# Revit family: Hager-FW-Surface_mounted-IP30-With_Cover-With_DIN-Hosted-AT-de
name_source: partatom
category: Electrical Equipment
units: mm (PartAtom-declared; Revit-internal decimal feet)

## family parameters
Cut with Voids When Loaded = No
Host = Face
Maintain Annotation Orientation = Yes
Panel Configuration = Two Columns, Circuits Across
Part Type = Panelboard
Room Calculation Point = No
Round Connector Dimension = Use Diameter
Shared = No

## types (12) — shared parameters
BC_MODEL_ID = 1554217
BC_OBJECT_ID = 513830
BC_OBJECT_VERSION = #3
Code hager = ADD-EC000214_EU
EF000003 - Montageart = Aufputz
EF000007 - Farbe = weiß
EF000024 - UV-beständig = No
EF000049 - Tiefe = 150 mm
EF000116 - RAL-Nummer = 9010
EF000118 - Mit Montageplatte = No
EF001062 - EMV-Ausführung = No
EF001088 - Anbaumöglichkeit = Yes
EF001134 - DIN-Schiene = Yes
EF004462 - Art der Schließung = sonstige
EF005474 - Schutzart (IP) = IP30
EF006244 - Transparenter Deckel/Tür = No
EF006306 - Mit Schloss = No
EF009212 - Ausführung Deckel = geschlossen
EF015776 - Erdungsklemmenblock = No
EF015777 - Neutralleiterklemmenblock = No
EF015941 - Signaldurchlassende Tür = No
ETIM class code = EC000214
ETIM class name = Small distribution board
HG000001-Anzahl der Spalten = 1
HG000002-Mit tür = Yes
HG000003-Bereich = FW
HG000005-Dicke = 2 mm  [stored 0.00656168 ft]
HG000006-Unterputz = No
HG000009-Doppelflügeligen Tür = No
HG000010-Asymmetrische Türen = No
HG000011-Leere Reihen von unten = No
HG000012-Türschwenkwinkel = 90.00°
HG000013-Tür links = No
HG000014-Tür rechts = Yes
HG000015-Sichtbarkeit der Türöffnung = Yes
HG000016-3D-Türsichtbarkeit = Yes
HG000017-Distanz zwischen den Polen = 18 mm  [stored 0.0590551 ft]
HG000060-RAL-number = 9010
HG000099-Onfly Template ID-de-AT = 507532
Manufacturer = Hager
Name = FW-Surface_mounted-IP30-With_Cover-With_DIN-AT
Name BIM&CO = Electricity
Name hager = ADD_Enclosures_EC000214
Uniformat = Low Tension Service & Dist.
Uniformat code = D501001
zero-valued in all types: Default Elevation, EF000218 - Einbautiefe, EF000332 - Einbauhöhe, EF000846 - Einbaubreite, EF001131 - Innentiefe, HG000007-Anzahl der leeren Spalten, HG000008-Anzahl der leeren Reihen

## per-type parameters (varying)
| type | BC_VARIANT_ID | EF000008 - Breite | EF000040 - Höhe | EF000266 - Anzahl der Reihen | EF002950 - Breite in Teilungseinheiten | HG000004-Herstellerreferenz | HGEF000266-Anzahl der Reihen | HGEF0002950-Breite in Teilungseinheiten |
| FW-Surface_mounted_W355_H641_D150_12_Modular_Spacing-FW312W | 1178707 | 355 mm | 641 mm  [stored 2.10302 ft] | 3 | 12 | FW312W | 3 | 12 |
| FW-Surface_mounted_W571_H641_D150_24_Modular_Spacing-FW324W | 1178708 | 571 mm  [stored 1.87336 ft] | 641 mm  [stored 2.10302 ft] | 3 | 24 | FW324W | 3 | 24 |
| FW-Surface_mounted_W355_H791_D150_12_Modular_Spacing-FW412W | 1178709 | 355 mm | 791 mm | 4 | 12 | FW412W | 4 | 12 |
| FW-Surface_mounted_W571_H791_D150_24_Modular_Spacing-FW424W | 1178710 | 571 mm  [stored 1.87336 ft] | 791 mm | 4 | 24 | FW424W | 4 | 24 |
| FW-Surface_mounted_W787_H791_D150_36_Modular_Spacing-FW436W | 1178711 | 787 mm  [stored 2.58202 ft] | 791 mm | 4 | 36 | FW436W | 4 | 36 |
| FW-Surface_mounted_W355_H941_D150_12_Modular_Spacing-FW512W | 1178712 | 355 mm | 941 mm | 5 | 12 | FW512W | 5 | 12 |
| FW-Surface_mounted_W571_H941_D150_24_Modular_Spacing-FW524W | 1178713 | 571 mm  [stored 1.87336 ft] | 941 mm | 5 | 24 | FW524W | 5 | 24 |
| FW-Surface_mounted_W787_H941_D150_36_Modular_Spacing-FW536W | 1178714 | 787 mm  [stored 2.58202 ft] | 941 mm | 5 | 36 | FW536W | 5 | 36 |
| FW-Surface_mounted_W355_H1091_D150_12_Modular_Spacing-FW612W | 1178715 | 355 mm | 1091 mm | 6 | 12 | FW612W | 6 | 12 |
| FW-Surface_mounted_W571_H1091_D150_24_Modular_Spacing-FW624W | 1178716 | 571 mm  [stored 1.87336 ft] | 1091 mm | 6 | 24 | FW624W | 6 | 24 |
| FW-Surface_mounted_W787_H1091_D150_36_Modular_Spacing-FW636W | 1178717 | 787 mm  [stored 2.58202 ft] | 1091 mm | 6 | 36 | FW636W | 6 | 36 |
| FW-Surface_mounted_W787_H1241_D150_36_Modular_Spacing-FW736W | 1178718 | 787 mm  [stored 2.58202 ft] | 1241 mm  [stored 4.07152 ft] | 7 | 36 | FW736W | 7 | 36 |

note: column(s) folded — value = type name in every type: Reference

note: [stored X ft] marks values corroborated as IEEE doubles in the binary element streams (Revit-internal decimal feet)

## geometry (parser evidence)
native form markers: Sweep x16
no freeform markers — native parametric forms only
